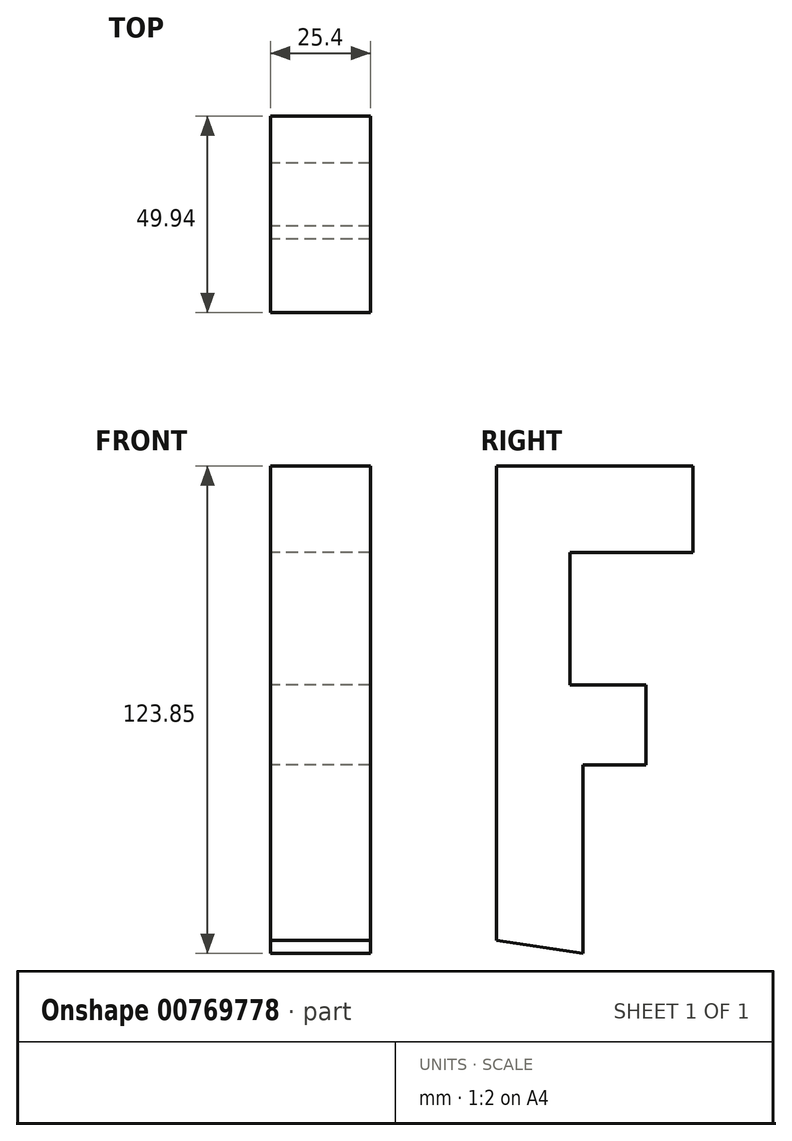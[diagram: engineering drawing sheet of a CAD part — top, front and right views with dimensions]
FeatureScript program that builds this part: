
annotation { "Feature Type Name" : "Feature", "Feature Type Description" : "" }
export const myFeature = defineFeature(function(context is Context, id is Id, definition is map)
    precondition{}
    {
        {
            var Q0;
            Q0=qCreatedBy(makeId("Right.planeOp"),FACE);
            var sketch = newSketch(context, id + "F0", { "sketchPlane" : qUnion([Q0])});
            skLineSegment(sketch, "E0", {"start": v(-60.26, -64.92) * mm, "end": v(-60.26, 55.6) * mm});
            skLineSegment(sketch, "E1", {"start": v(-60.26, 55.6) * mm, "end": v(-10.32, 55.6) * mm});
            skLineSegment(sketch, "E2", {"start": v(-10.32, 55.6) * mm, "end": v(-10.32, 33.62) * mm});
            skLineSegment(sketch, "E3", {"start": v(-10.32, 33.62) * mm, "end": v(-41.61, 33.62) * mm});
            skLineSegment(sketch, "E4", {"start": v(-41.61, 33.62) * mm, "end": v(-41.61, 0) * mm});
            skLineSegment(sketch, "E5", {"start": v(-41.61, 0) * mm, "end": v(-22.3, 0) * mm});
            skLineSegment(sketch, "E6", {"start": v(-22.3, 0) * mm, "end": v(-22.3, -20.3) * mm});
            skLineSegment(sketch, "E7", {"start": v(-22.3, -20.3) * mm, "end": v(-38.29, -20.3) * mm});
            skLineSegment(sketch, "E8", {"start": v(-38.29, -20.3) * mm, "end": v(-38.29, -68.25) * mm});
            skLineSegment(sketch, "E9", {"start": v(-38.29, -68.25) * mm, "end": v(-60.26, -64.92) * mm});
            skSolve(sketch);
        }
        {
            var Q0;
            Q0 = qSketchRegion(id + "F0", true);
            extrude(context, id + "F1", {"entities" : qUnion([Q0]), "depth" : 25.4 * mm, "offsetDistance" : 25.4 * mm});
        }
    });
